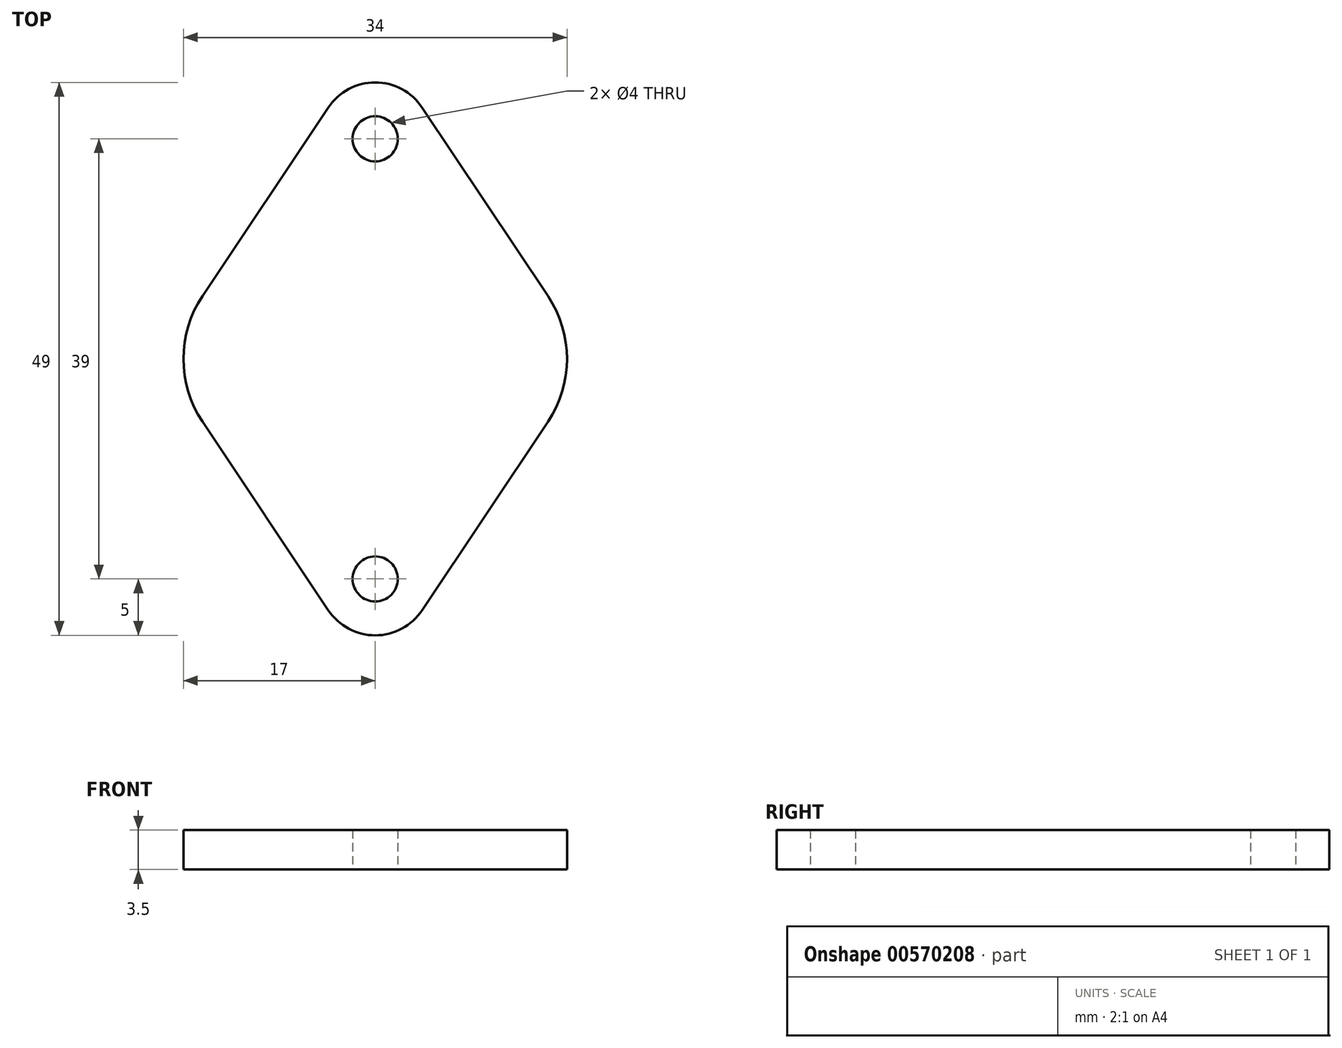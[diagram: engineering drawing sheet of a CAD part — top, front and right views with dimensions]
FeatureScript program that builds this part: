
annotation { "Feature Type Name" : "Feature", "Feature Type Description" : "" }
export const myFeature = defineFeature(function(context is Context, id is Id, definition is map)
    precondition{}
    {
        {
            var Q0;
            Q0=qCreatedBy(makeId("Top.planeOp"),FACE);
            var sketch = newSketch(context, id + "F0", { "sketchPlane" : qUnion([Q0])});
            skLineSegment(sketch, "E0", {"start": v(-15.32, 5.55) * mm, "end": v(-4.16, 22.28) * mm});
            skLineSegment(sketch, "E1", {"start": v(4.16, 22.28) * mm, "end": v(15.32, 5.55) * mm});
            skLineSegment(sketch, "E2", {"start": v(15.32, -5.55) * mm, "end": v(4.16, -22.28) * mm});
            skLineSegment(sketch, "E3", {"start": v(-4.16, -22.28) * mm, "end": v(-15.32, -5.55) * mm});
            skLineSegment(sketch, "E4", {"start": v(0, 0) * mm, "end": v(19.02, 0) * mm, "construction": true});
            skLineSegment(sketch, "E5", {"start": v(-19.02, 0) * mm, "end": v(0, 0) * mm, "construction": true});
            skLineSegment(sketch, "E6", {"start": v(0, 28.5) * mm, "end": v(0, 0) * mm, "construction": true});
            skLineSegment(sketch, "E7", {"start": v(0, -28.5) * mm, "end": v(0, 0) * mm, "construction": true});
            skPoint(sketch, "E8.visualSharp", {"position": v(-19.02, 0) * mm});
            skArc(sketch, "E8.filletArc", {"start": v(-15.32, 5.55) * mm, "mid": v(-17, 0) * mm, "end": v(-15.32, -5.55) * mm});
            skPoint(sketch, "E9.visualSharp", {"position": v(19.02, 0) * mm});
            skArc(sketch, "E9.filletArc", {"start": v(15.32, -5.55) * mm, "mid": v(17, 0) * mm, "end": v(15.32, 5.55) * mm});
            skPoint(sketch, "E10.visualSharp", {"position": v(0, 28.5) * mm});
            skArc(sketch, "E10.filletArc", {"start": v(4.16, 22.28) * mm, "mid": v(0, 24.5) * mm, "end": v(-4.16, 22.28) * mm});
            skPoint(sketch, "E11.visualSharp", {"position": v(0, -28.5) * mm});
            skArc(sketch, "E11.filletArc", {"start": v(-4.16, -22.28) * mm, "mid": v(0, -24.5) * mm, "end": v(4.16, -22.28) * mm});
            skPoint(sketch, "E12", {"position": v(17, 0) * mm});
            skPoint(sketch, "E13", {"position": v(-17, 0) * mm});
            skCircle(sketch, "E14", {"center": v(0, 19.5) * mm, "radius": 2 * mm});
            skCircle(sketch, "E15", {"center": v(0, -19.5) * mm, "radius": 2 * mm});
            skSolve(sketch);
        }
        {
            var Q0;
            Q0=makeQuery(id+"F0.imprint","IMPRINT",FACE,{"disambiguationData":[TD([[makeQuery(id+"F0.imprint","IMPRINT",EDGE,{"derivedFrom":sQuery(id+"F0.wireOp",EDGE,"E0")}),-1.0]])]});
            extrude(context, id + "F1", {"entities" : qUnion([Q0]), "depth" : 3.5 * mm, "offsetDistance" : 25 * mm});
        }
    });
